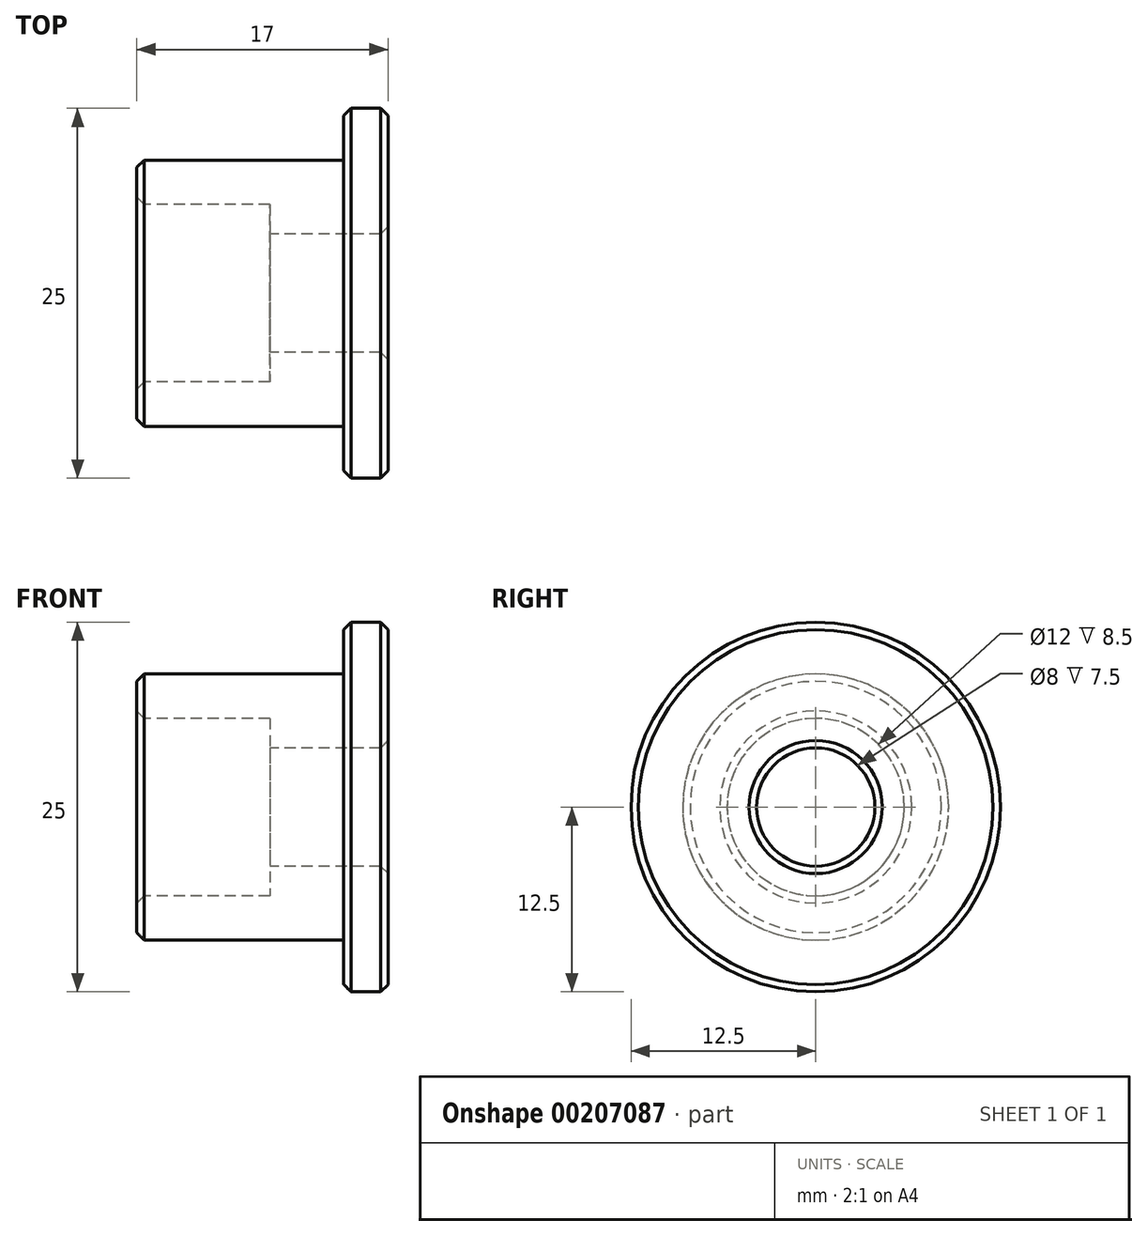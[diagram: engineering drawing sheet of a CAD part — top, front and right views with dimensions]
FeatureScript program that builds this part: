
annotation { "Feature Type Name" : "Feature", "Feature Type Description" : "" }
export const myFeature = defineFeature(function(context is Context, id is Id, definition is map)
    precondition{}
    {
        {
            var Q0;
            Q0=qCreatedBy(makeId("Front.planeOp"),FACE);
            var sketch = newSketch(context, id + "F0", { "sketchPlane" : qUnion([Q0])});
            skLineSegment(sketch, "E0", {"start": v(-9.88, 0) * mm, "end": v(10.12, 0) * mm, "construction": true});
            skLineSegment(sketch, "E1", {"start": v(-9, 6) * mm, "end": v(0, 6) * mm});
            skLineSegment(sketch, "E2", {"start": v(0, 6) * mm, "end": v(0, 4) * mm});
            skLineSegment(sketch, "E3", {"start": v(0, 4) * mm, "end": v(8, 4) * mm});
            skLineSegment(sketch, "E4", {"start": v(8, 4) * mm, "end": v(8, 12.5) * mm});
            skLineSegment(sketch, "E5", {"start": v(8, 12.5) * mm, "end": v(5, 12.5) * mm});
            skLineSegment(sketch, "E6", {"start": v(5, 12.5) * mm, "end": v(5, 9) * mm});
            skLineSegment(sketch, "E7", {"start": v(5, 9) * mm, "end": v(-9, 9) * mm});
            skLineSegment(sketch, "E8", {"start": v(-9, 9) * mm, "end": v(-9, 6) * mm});
            skSolve(sketch);
        }
        {
            var Q0;
            Q0 = qSketchRegion(id + "F0", true);
            var Q1;
            Q1=sQuery(id+"F0.wireOp",EDGE,"E0");
            revolve(context, id + "F2", {"entities" : qUnion([Q0]), "axis" : qUnion([Q1]), "revolveType" : RevolveType.FULL});
        }
        {
            var Q0;
            Q0=makeQuery(id+"F2.opRevolve","SWEPT_EDGE",EDGE,{"disambiguationData":[OSD([sQuery(id+"F0.wireOp",EDGE,"E1"),sQuery(id+"F0.wireOp",EDGE,"E8")])]});
            var Q1;
            Q1=makeQuery(id+"F2.opRevolve","SWEPT_EDGE",EDGE,{"disambiguationData":[OSD([sQuery(id+"F0.wireOp",EDGE,"E7"),sQuery(id+"F0.wireOp",EDGE,"E8")])]});
            var Q2;
            Q2=makeQuery(id+"F2.opRevolve","SWEPT_EDGE",EDGE,{"disambiguationData":[OSD([sQuery(id+"F0.wireOp",EDGE,"E5"),sQuery(id+"F0.wireOp",EDGE,"E6")])]});
            var Q3;
            Q3=makeQuery(id+"F2.opRevolve","SWEPT_EDGE",EDGE,{"disambiguationData":[OSD([sQuery(id+"F0.wireOp",EDGE,"E4"),sQuery(id+"F0.wireOp",EDGE,"E5")])]});
            var Q4;
            Q4=makeQuery(id+"F2.opRevolve","SWEPT_EDGE",EDGE,{"disambiguationData":[OSD([sQuery(id+"F0.wireOp",EDGE,"E3"),sQuery(id+"F0.wireOp",EDGE,"E4")])]});
            chamfer(context, id + "F1", {"entities" : qUnion([Q0, Q1, Q2, Q3, Q4]), "width" : 0.5 * mm, "tangentPropagation" : true});
        }
    });
